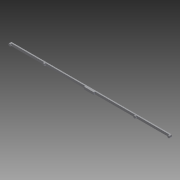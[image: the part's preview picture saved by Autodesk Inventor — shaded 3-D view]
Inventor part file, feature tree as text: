
AUTODESK INVENTOR PART (.ipt)
format: ipt  version: 2011 (Build 150239000, 239)  size: 91,136 bytes
history: native  units: in
note: dims shown in document units (in); Inventor stores cm internally (conversion verified against a paired STEP export)
features: extrude x2, sketch x2
ambient origin geometry x8: Origin, YZ Plane, XZ Plane, XY Plane, X Axis, Y Axis, Z Axis, Center Point
bodies: Solid1 (feature_tree)
feature tree (4):
  extrude  "Extrusion1"  Depth=0.25in
  extrude  "Extrusion2"  Depth=3.531in
  sketch  "Sketch1"  dims[d0=16.531in d1=0.25in]
  sketch  "Sketch2"  dims[d2=0.125in d3=0.0in d4=3.531in d5=3.531in d6=0.5in d7=1.0in d8=0.125in d9=0.0in]
